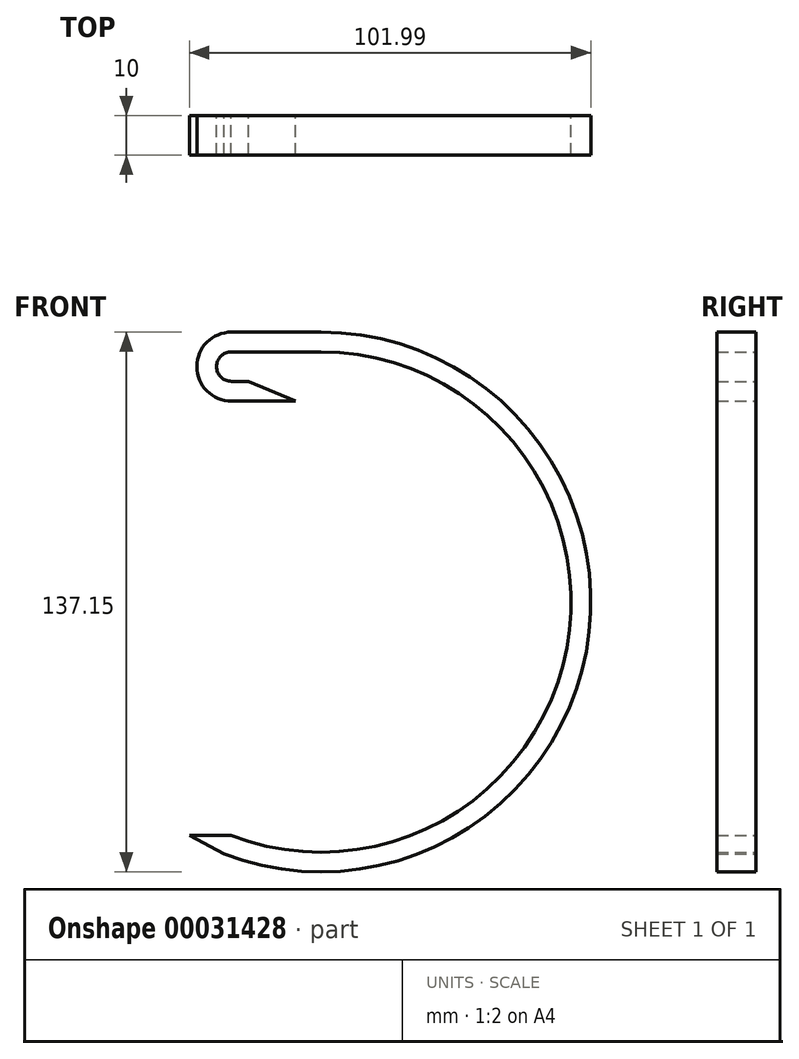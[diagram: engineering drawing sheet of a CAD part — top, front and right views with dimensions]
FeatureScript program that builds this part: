
annotation { "Feature Type Name" : "Feature", "Feature Type Description" : "" }
export const myFeature = defineFeature(function(context is Context, id is Id, definition is map)
    precondition{}
    {
        {
            var Q0;
            Q0=qCreatedBy(makeId("Front.planeOp"),FACE);
            var sketch = newSketch(context, id + "F0", { "sketchPlane" : qUnion([Q0])});
            skArc(sketch, "E0", {"start": v(-10.92, 15.9) * mm, "mid": v(56.5, -65.22) * mm, "end": v(-35.58, -116.66) * mm});
            skArc(sketch, "E1.0", {"start": v(-10.92, 10.9) * mm, "mid": v(51.58, -64.3) * mm, "end": v(-33.78, -112) * mm});
            skLineSegment(sketch, "E2", {"start": v(-33.78, -112) * mm, "end": v(-44.34, -112) * mm});
            skLineSegment(sketch, "E3", {"start": v(-44.34, -112) * mm, "end": v(-35.58, -116.66) * mm});
            skLineSegment(sketch, "E4", {"start": v(-10.92, 15.9) * mm, "end": v(-33.68, 15.9) * mm});
            skLineSegment(sketch, "E5", {"start": v(-10.92, 10.9) * mm, "end": v(-33.68, 10.9) * mm});
            skArc(sketch, "E6", {"start": v(-33.68, 10.9) * mm, "mid": v(-37.43, 7.14) * mm, "end": v(-33.68, 3.39) * mm});
            skArc(sketch, "E7.0", {"start": v(-33.68, 15.9) * mm, "mid": v(-42.43, 7.14) * mm, "end": v(-33.68, -1.61) * mm});
            skLineSegment(sketch, "E8", {"start": v(-33.68, 3.39) * mm, "end": v(-29.3, 3.39) * mm});
            skLineSegment(sketch, "E9", {"start": v(-33.68, -1.61) * mm, "end": v(-29.3, -1.61) * mm});
            skLineSegment(sketch, "E10", {"start": v(-29.3, -1.61) * mm, "end": v(-17.38, -1.61) * mm});
            skLineSegment(sketch, "E11", {"start": v(-17.38, -1.61) * mm, "end": v(-29.3, 3.39) * mm});
            skSolve(sketch);
        }
        {
            var Q0;
            Q0 = qSketchRegion(id + "F0", true);
            extrude(context, id + "F1", {"entities" : qUnion([Q0]), "depth" : 10 * mm});
        }
    });
